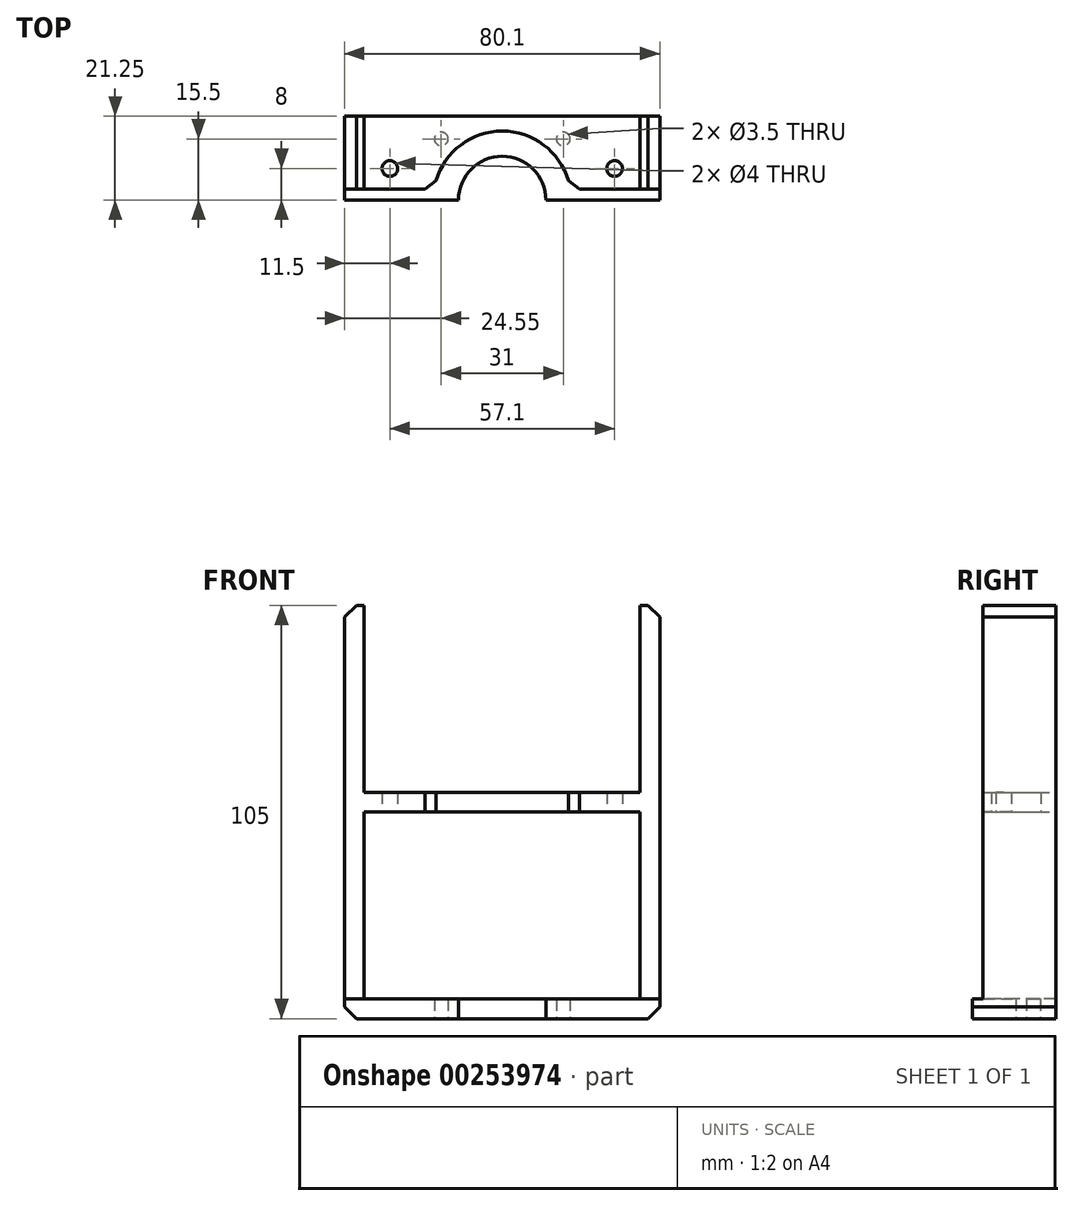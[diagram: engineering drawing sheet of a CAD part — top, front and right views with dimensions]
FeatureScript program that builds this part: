
annotation { "Feature Type Name" : "Feature", "Feature Type Description" : "" }
export const myFeature = defineFeature(function(context is Context, id is Id, definition is map)
    precondition{}
    {
        {
            var Q0;
            Q0=qCreatedBy(makeId("Top.planeOp"),FACE);
            var sketch = newSketch(context, id + "F0", { "sketchPlane" : qUnion([Q0])});
            skArc(sketch, "E0", {"start": v(11.1, 0) * mm, "mid": v(0, 11.1) * mm, "end": v(-11.1, 0) * mm});
            skLineSegment(sketch, "E1.top", {"start": v(-40.05, 21.25) * mm, "end": v(40.05, 21.25) * mm});
            skLineSegment(sketch, "E1.left", {"start": v(-40.05, 0) * mm, "end": v(-40.05, 21.25) * mm});
            skLineSegment(sketch, "E1.right", {"start": v(40.05, 0) * mm, "end": v(40.05, 21.25) * mm});
            skLineSegment(sketch, "E2.bottom", {"start": v(-15.5, -15.5) * mm, "end": v(15.5, -15.5) * mm, "construction": true});
            skLineSegment(sketch, "E2.top", {"start": v(-15.5, 15.5) * mm, "end": v(15.5, 15.5) * mm, "construction": true});
            skLineSegment(sketch, "E2.left", {"start": v(-15.5, -15.5) * mm, "end": v(-15.5, 15.5) * mm, "construction": true});
            skLineSegment(sketch, "E2.right", {"start": v(15.5, -15.5) * mm, "end": v(15.5, 15.5) * mm, "construction": true});
            skCircle(sketch, "E3", {"center": v(-15.5, 15.5) * mm, "radius": 1.75 * mm});
            skCircle(sketch, "E4", {"center": v(15.5, 15.5) * mm, "radius": 1.75 * mm});
            skLineSegment(sketch, "E5", {"start": v(-40.05, 0) * mm, "end": v(-11.1, 0) * mm});
            skPoint(sketch, "E5.endSnap0", {"position": v(-15.5, 0) * mm});
            skLineSegment(sketch, "E6", {"start": v(40.05, 0) * mm, "end": v(11.1, 0) * mm});
            skPoint(sketch, "E6.endSnap0", {"position": v(15.5, 0) * mm});
            skPoint(sketch, "E1.bottom.start.orphan", {"position": v(-40.05, -21.25) * mm});
            skPoint(sketch, "E7.orphan", {"position": v(40.05, -21.25) * mm});
            skSolve(sketch);
        }
        {
            var Q0;
            Q0 = qSketchRegion(id + "F0", true);
            extrude(context, id + "F1", {"entities" : qUnion([Q0]), "depth" : 5 * mm});
        }
        {
            var Q0;
            Q0=makeQuery(id+"F1.opExtrude","CAP_FACE",FACE,{"disambiguationData":[OSD([sQuery(id+"F0.wireOp",EDGE,"E0"),sQuery(id+"F0.wireOp",EDGE,"E1.top"),sQuery(id+"F0.wireOp",EDGE,"E1.left"),sQuery(id+"F0.wireOp",EDGE,"E1.right"),sQuery(id+"F0.wireOp",EDGE,"E3"),sQuery(id+"F0.wireOp",EDGE,"E4"),sQuery(id+"F0.wireOp",EDGE,"E5"),sQuery(id+"F0.wireOp",EDGE,"E6")])],"isStart":false});
            var sketch = newSketch(context, id + "F2", { "sketchPlane" : qUnion([Q0])});
            skLineSegment(sketch, "E8.bottom", {"start": v(-40.05, 21.25) * mm, "end": v(-35.05, 21.25) * mm});
            skLineSegment(sketch, "E8.top", {"start": v(-40.05, 2.75) * mm, "end": v(-35.05, 2.75) * mm});
            skLineSegment(sketch, "E8.left", {"start": v(-40.05, 21.25) * mm, "end": v(-40.05, 2.75) * mm});
            skLineSegment(sketch, "E8.right", {"start": v(-35.05, 21.25) * mm, "end": v(-35.05, 2.75) * mm});
            skLineSegment(sketch, "E9.bottom", {"start": v(40.05, 21.25) * mm, "end": v(35.05, 21.25) * mm});
            skLineSegment(sketch, "E9.top", {"start": v(40.05, 2.75) * mm, "end": v(35.05, 2.75) * mm});
            skLineSegment(sketch, "E9.left", {"start": v(40.05, 21.25) * mm, "end": v(40.05, 2.75) * mm});
            skLineSegment(sketch, "E9.right", {"start": v(35.05, 21.25) * mm, "end": v(35.05, 2.75) * mm});
            skSolve(sketch);
        }
        {
            var Q0;
            Q0 = qSketchRegion(id + "F2", true);
            extrude(context, id + "F3", {"entities" : qUnion([Q0]), "operationType" : NewBodyOperationType.ADD, "depth" : 100 * mm});
        }
        {
            var Q0;
            Q0=makeQuery(id+"F3.opExtrude","SWEPT_FACE",FACE,{"disambiguationData":[OSD([sQuery(id+"F2.wireOp",EDGE,"E9.right")])]});
            var sketch = newSketch(context, id + "F4", { "sketchPlane" : qUnion([Q0])});
            skLineSegment(sketch, "E10", {"start": v(-12, 5) * mm, "end": v(-12, 57.5) * mm, "construction": true});
            skLineSegment(sketch, "E11.0", {"start": v(-21.25, 105) * mm, "end": v(-21.25, 5) * mm, "construction": true});
            skPoint(sketch, "E12", {"position": v(-21.25, 57.5) * mm});
            skLineSegment(sketch, "E13.bottom", {"start": v(-21.25, 57.5) * mm, "end": v(-2.75, 57.5) * mm});
            skLineSegment(sketch, "E13.top", {"start": v(-21.25, 52.5) * mm, "end": v(-2.75, 52.5) * mm});
            skLineSegment(sketch, "E13.left", {"start": v(-21.25, 57.5) * mm, "end": v(-21.25, 52.5) * mm});
            skLineSegment(sketch, "E13.right", {"start": v(-2.75, 57.5) * mm, "end": v(-2.75, 52.5) * mm});
            skSolve(sketch);
        }
        {
            var Q0;
            Q0 = qSketchRegion(id + "F4", true);
            extrude(context, id + "F5", {"entities" : qUnion([Q0]), "operationType" : NewBodyOperationType.ADD, "endBound" : BoundingType.UP_TO_NEXT, "depth" : 25 * mm});
        }
        {
            var Q0;
            Q0=makeQuery(id+"F5.opExtrude","SWEPT_FACE",FACE,{"disambiguationData":[OSD([sQuery(id+"F4.wireOp",EDGE,"E13.top")])]});
            var sketch = newSketch(context, id + "F6", { "sketchPlane" : qUnion([Q0])});
            skLineSegment(sketch, "E14.0", {"start": v(-35.05, -2.75) * mm, "end": v(35.05, -2.75) * mm, "construction": true});
            skLineSegment(sketch, "E15.0", {"start": v(-35.05, -2.75) * mm, "end": v(-35.05, -21.25) * mm, "construction": true});
            skLineSegment(sketch, "E16.0", {"start": v(35.05, -21.25) * mm, "end": v(35.05, -2.75) * mm, "construction": true});
            skCircle(sketch, "E17", {"center": v(0, 0) * mm, "radius": 17.5 * mm});
            skPoint(sketch, "E18.trimOffspring.end.orphan", {"position": v(-11.1, 0) * mm});
            skPoint(sketch, "E19.0.start.orphan", {"position": v(11.1, 0) * mm});
            skLineSegment(sketch, "E20", {"start": v(-35.05, 0) * mm, "end": v(-35.05, -2.75) * mm, "construction": true});
            skLineSegment(sketch, "E21", {"start": v(-35.05, 0) * mm, "end": v(0, 0) * mm, "construction": true});
            skLineSegment(sketch, "E22", {"start": v(-35.05, -8) * mm, "end": v(-28.55, -8) * mm, "construction": true});
            skLineSegment(sketch, "E23", {"start": v(-28.55, -8) * mm, "end": v(-28.55, 0) * mm, "construction": true});
            skCircle(sketch, "E24", {"center": v(-28.55, -8) * mm, "radius": 2 * mm});
            skLineSegment(sketch, "E25", {"start": v(0, 0) * mm, "end": v(0, -22.66) * mm, "construction": true});
            skPoint(sketch, "E25.endSnap0", {"position": v(0, -21.25) * mm});
            skCircle(sketch, "E26.MirrorC", {"center": v(28.55, -8) * mm, "radius": 2 * mm});
            skSolve(sketch);
        }
        {
            var Q0;
            Q0 = qSketchRegion(id + "F6", true);
            extrude(context, id + "F7", {"entities" : qUnion([Q0]), "operationType" : NewBodyOperationType.REMOVE, "oppositeDirection" : true, "depth" : 25 * mm});
        }
        {
            var Q0;
            Q0=makeQuery(id+"F1.opExtrude","CAP_EDGE",EDGE,{"disambiguationData":[OSD([sQuery(id+"F0.wireOp",EDGE,"E1.left")])],"isStart":true});
            var Q1;
            Q1=makeQuery(id+"F1.opExtrude","CAP_EDGE",EDGE,{"disambiguationData":[OSD([sQuery(id+"F0.wireOp",EDGE,"E1.right")])],"isStart":true});
            var Q2;
            Q2=makeQuery(id+"F3.opExtrude","CAP_EDGE",EDGE,{"disambiguationData":[OSD([sQuery(id+"F2.wireOp",EDGE,"E8.left")])],"isStart":false});
            var Q3;
            Q3=makeQuery(id+"F3.opExtrude","CAP_EDGE",EDGE,{"disambiguationData":[OSD([sQuery(id+"F2.wireOp",EDGE,"E9.left")])],"isStart":false});
            chamfer(context, id + "F8", {"entities" : qUnion([Q0, Q1, Q2, Q3]), "width" : 3 * mm, "tangentPropagation" : true});
        }
        {
            var Q0;
            Q0=makeQuery(id+"F7.boolean.opBoolean","INTERSECT",EDGE,{"disambiguationData":[OD(1.0)],"derivedFrom":[makeQuery(id+"F5.boolean.opBoolean","MERGE",FACE,{"derivedFrom":[makeQuery(id+"F3.opExtrude","SWEPT_FACE",FACE,{"disambiguationData":[OSD([sQuery(id+"F2.wireOp",EDGE,"E8.top")])]}),makeQuery(id+"F3.opExtrude","SWEPT_FACE",FACE,{"disambiguationData":[OSD([sQuery(id+"F2.wireOp",EDGE,"E9.top")])]}),makeQuery(id+"F5.opExtrude","SWEPT_FACE",FACE,{"disambiguationData":[OSD([sQuery(id+"F4.wireOp",EDGE,"E13.right")])]})]}),makeQuery(id+"F7.opExtrude","SWEPT_FACE",FACE,{"disambiguationData":[OSD([sQuery(id+"F6.wireOp",EDGE,"E17")])]})]});
            var Q1;
            Q1=makeQuery(id+"F7.boolean.opBoolean","INTERSECT",EDGE,{"disambiguationData":[OD(0.0)],"derivedFrom":[makeQuery(id+"F5.boolean.opBoolean","MERGE",FACE,{"derivedFrom":[makeQuery(id+"F3.opExtrude","SWEPT_FACE",FACE,{"disambiguationData":[OSD([sQuery(id+"F2.wireOp",EDGE,"E8.top")])]}),makeQuery(id+"F3.opExtrude","SWEPT_FACE",FACE,{"disambiguationData":[OSD([sQuery(id+"F2.wireOp",EDGE,"E9.top")])]}),makeQuery(id+"F5.opExtrude","SWEPT_FACE",FACE,{"disambiguationData":[OSD([sQuery(id+"F4.wireOp",EDGE,"E13.right")])]})]}),makeQuery(id+"F7.opExtrude","SWEPT_FACE",FACE,{"disambiguationData":[OSD([sQuery(id+"F6.wireOp",EDGE,"E17")])]})]});
            chamfer(context, id + "F9", {"entities" : qUnion([Q0, Q1]), "width" : 3 * mm, "tangentPropagation" : true});
        }
    });
